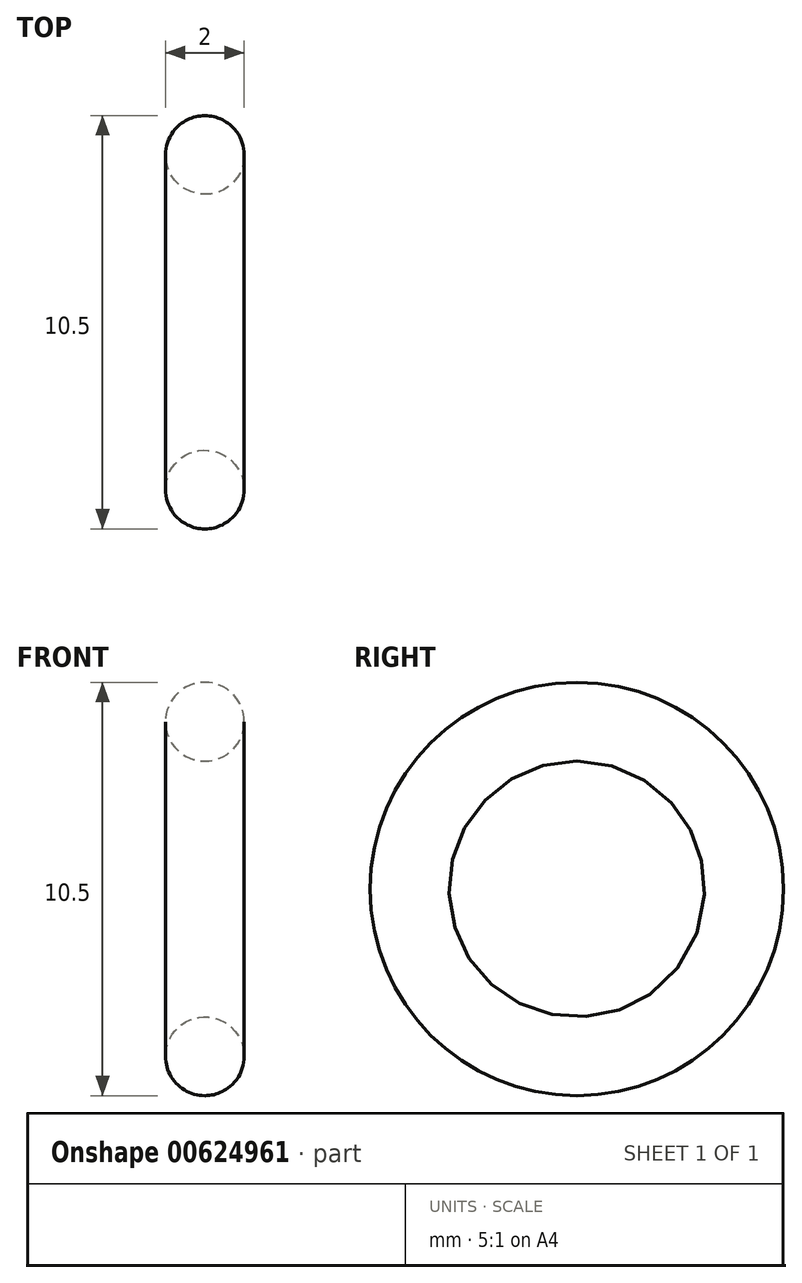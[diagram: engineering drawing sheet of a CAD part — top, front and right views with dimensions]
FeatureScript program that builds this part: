
annotation { "Feature Type Name" : "Feature", "Feature Type Description" : "" }
export const myFeature = defineFeature(function(context is Context, id is Id, definition is map)
    precondition{}
    {
        {
            var Q0;
            Q0=qCreatedBy(makeId("Front.planeOp"),FACE);
            var sketch = newSketch(context, id + "F0", { "sketchPlane" : qUnion([Q0])});
            skCircle(sketch, "E0", {"center": v(0, 4.25) * mm, "radius": 1 * mm});
            skLineSegment(sketch, "E1", {"start": v(0, 0) * mm, "end": v(0, 4.25) * mm, "construction": true});
            skLineSegment(sketch, "E2", {"start": v(0, 0) * mm, "end": v(1.77, 0) * mm, "construction": true});
            skLineSegment(sketch, "E3", {"start": v(0, 3.25) * mm, "end": v(0.75, 3.25) * mm, "construction": true});
            skPoint(sketch, "E3.startSnap0", {"position": v(0, 2.12) * mm});
            skSolve(sketch);
        }
        {
            var Q0;
            Q0=makeQuery(id+"F0.imprint","IMPRINT",FACE,{"disambiguationData":[TD([[makeQuery(id+"F0.imprint","IMPRINT",EDGE,{"derivedFrom":sQuery(id+"F0.wireOp",EDGE,"E0")}),1.0]])]});
            var Q1;
            Q1=sQuery(id+"F0.wireOp",EDGE,"E2");
            revolve(context, id + "F1", {"entities" : qUnion([Q0]), "axis" : qUnion([Q1]), "revolveType" : RevolveType.FULL});
        }
    });
